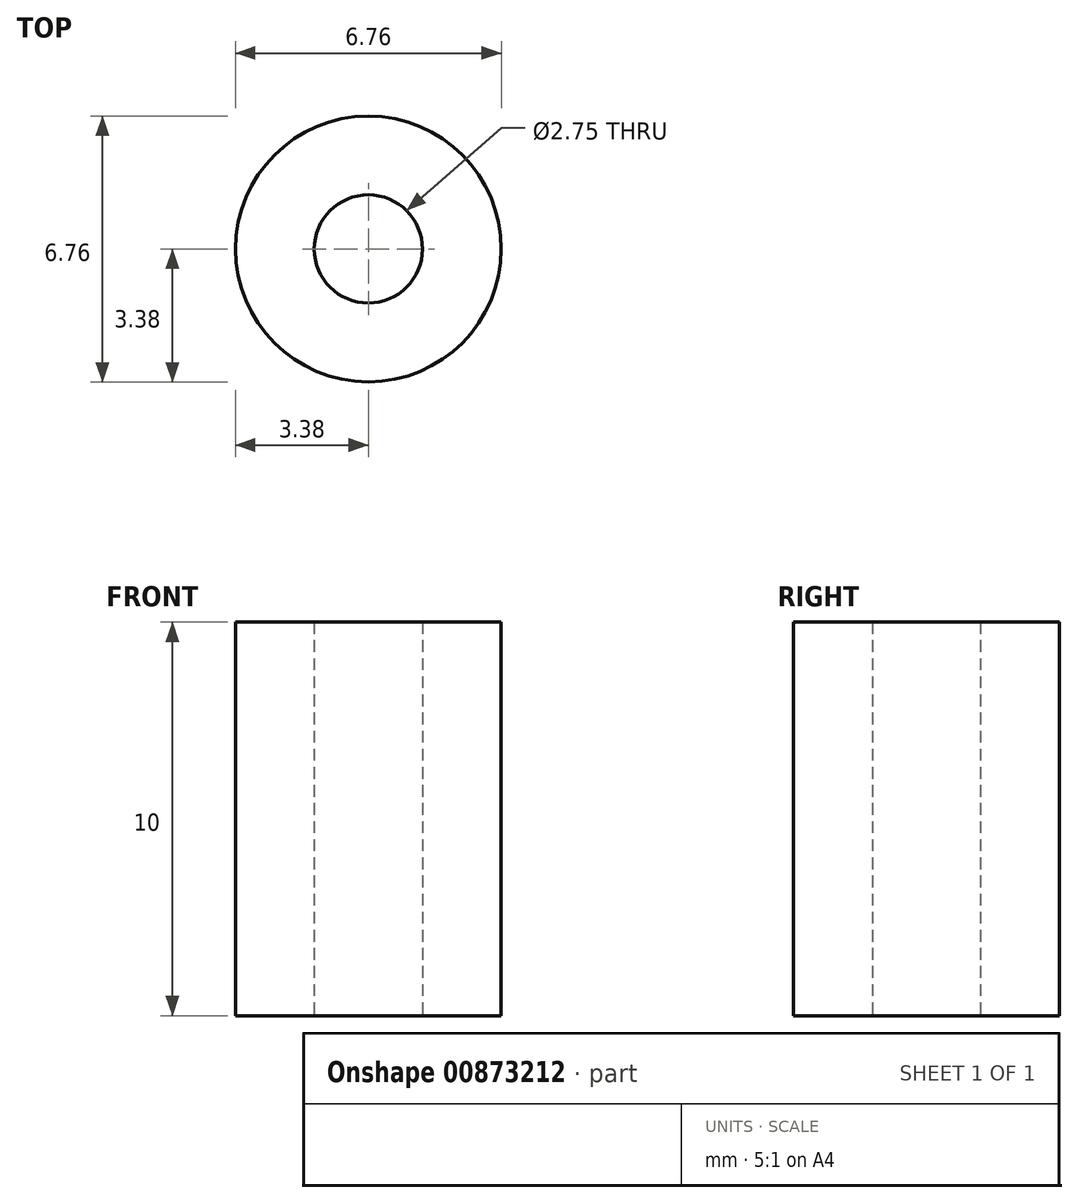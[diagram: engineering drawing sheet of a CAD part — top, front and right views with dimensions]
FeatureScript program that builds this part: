
annotation { "Feature Type Name" : "Feature", "Feature Type Description" : "" }
export const myFeature = defineFeature(function(context is Context, id is Id, definition is map)
    precondition{}
    {
        {
            var Q0;
            Q0=qCreatedBy(makeId("Top.planeOp"),FACE);
            var sketch = newSketch(context, id + "F0", { "sketchPlane" : qUnion([Q0])});
            skCircle(sketch, "E0", {"center": v(0, 0) * mm, "radius": 1.38 * mm});
            skCircle(sketch, "E1", {"center": v(0, 0) * mm, "radius": 3.38 * mm});
            skSolve(sketch);
        }
        {
            var Q0;
            Q0 = qSketchRegion(id + "F0", true);
            extrude(context, id + "F1", {"entities" : qUnion([Q0]), "depth" : 10 * mm, "offsetDistance" : 25 * mm});
        }
    });
